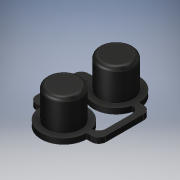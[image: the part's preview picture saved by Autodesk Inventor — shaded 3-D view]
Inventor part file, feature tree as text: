
AUTODESK INVENTOR PART (.ipt)
format: ipt  version: 2017 (Build 210142000, 142)  size: 185,856 bytes
history: native  units: in
note: dims shown in document units (in); Inventor stores cm internally (conversion verified against a paired STEP export)
features: extrude x3, sketch x3, fillet x1
ambient origin geometry x8: Origin, YZ Plane, XZ Plane, XY Plane, X Axis, Y Axis, Z Axis, Center Point
bodies: Solid1 (feature_tree)
feature tree (7):
  extrude  "Extrusion1"  Depth=0.39in
  extrude  "Extrusion2"  Depth=0.048in TaperAngle=0.0deg
  fillet  "Fillet1"  Radius=0.29in
  extrude  "Extrusion3"  Depth=0.45in
  sketch  "Sketch1"  dims[d0=0.39in d1=0.39in]
  sketch  "Sketch2"  dims[d2=0.45in d3=0.048in d4=0.0in d5=0.29in]
  sketch  "Sketch3"  dims[d6=0.29in d7=0.45in d8=0.265in d9=0.0in d10=0.0312in d12=0.05in d14=0.0625in d15=0.048in d16=0.0in d17=0.3in d18=0.05in d21=0.3in d22=0.05in d23=0.0501in]
